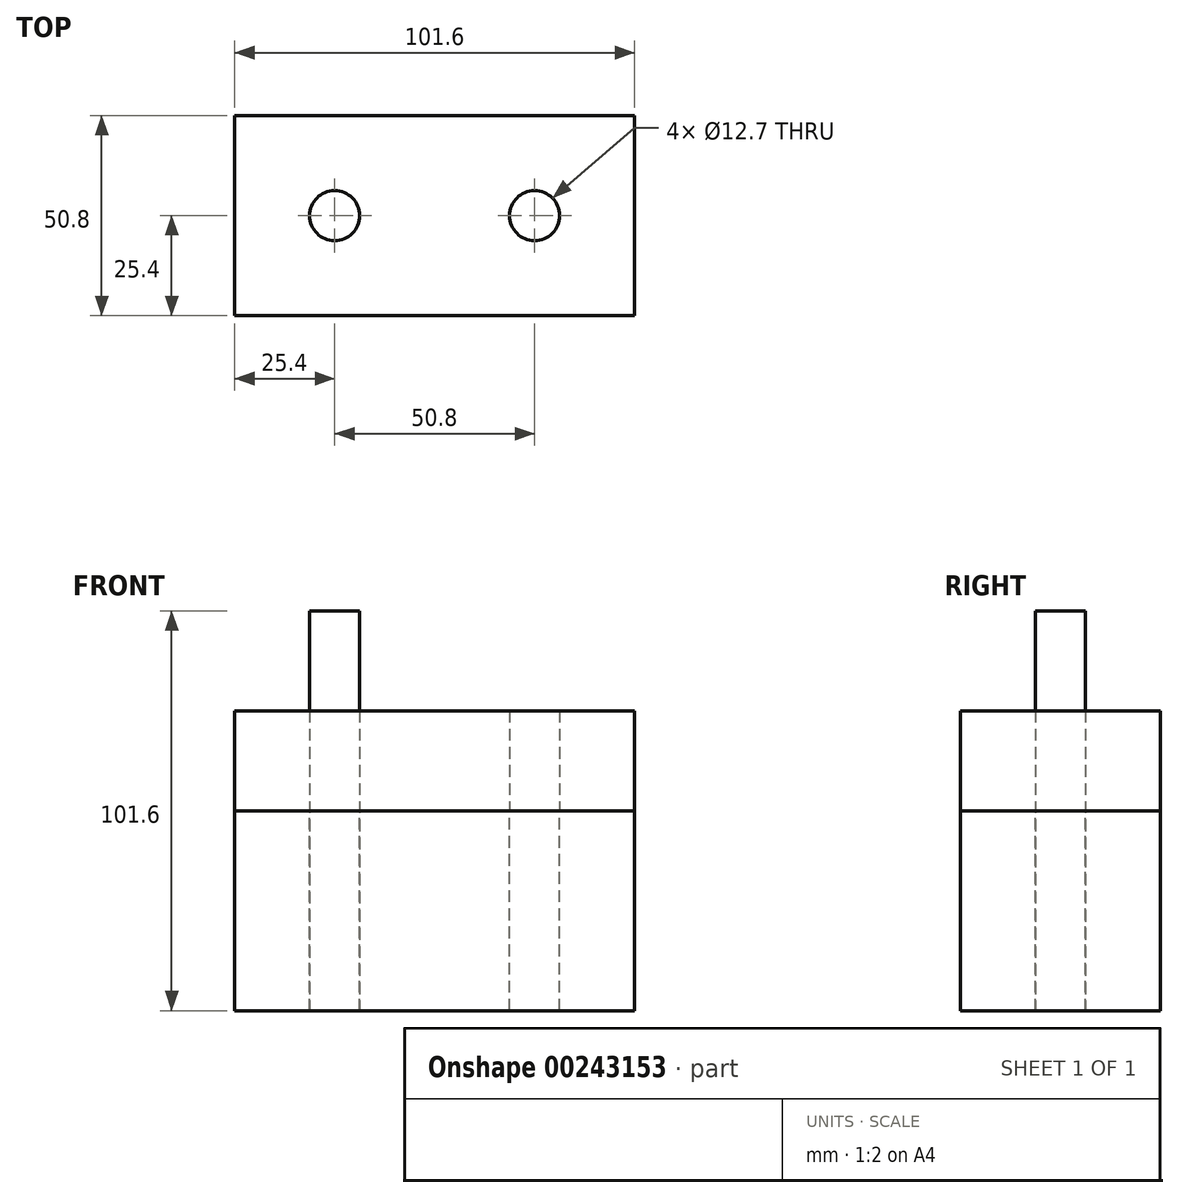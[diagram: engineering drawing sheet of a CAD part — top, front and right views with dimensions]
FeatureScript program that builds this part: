
annotation { "Feature Type Name" : "Feature", "Feature Type Description" : "" }
export const myFeature = defineFeature(function(context is Context, id is Id, definition is map)
    precondition{}
    {
        {
            var Q0;
            Q0=qCreatedBy(makeId("Top.planeOp"),FACE);
            var sketch = newSketch(context, id + "F0", { "sketchPlane" : qUnion([Q0])});
            skLineSegment(sketch, "E0.bottom", {"start": v(0, 0) * mm, "end": v(101.6, 0) * mm});
            skLineSegment(sketch, "E0.top", {"start": v(0, 50.8) * mm, "end": v(101.6, 50.8) * mm});
            skLineSegment(sketch, "E0.left", {"start": v(0, 0) * mm, "end": v(0, 50.8) * mm});
            skLineSegment(sketch, "E0.right", {"start": v(101.6, 0) * mm, "end": v(101.6, 50.8) * mm});
            skCircle(sketch, "E1", {"center": v(25.4, 25.4) * mm, "radius": 6.35 * mm});
            skPoint(sketch, "E1.centerSnap0", {"position": v(0, 25.4) * mm});
            skCircle(sketch, "E2", {"center": v(76.2, 25.4) * mm, "radius": 6.35 * mm});
            skSolve(sketch);
        }
        {
            var Q0;
            Q0 = qSketchRegion(id + "F0", true);
            extrude(context, id + "F1", {"entities" : qUnion([Q0]), "depth" : 25.4 * mm});
        }
        {
            var Q0;
            Q0 = qSketchRegion(id + "F0", true);
            extrude(context, id + "F2", {"entities" : qUnion([Q0]), "oppositeDirection" : true, "depth" : 50.8 * mm});
        }
        {
            var Q0;
            Q0=makeQuery(id+"F2.opExtrude","CAP_FACE",FACE,{"disambiguationData":[OSD([sQuery(id+"F0.wireOp",EDGE,"E0.bottom"),sQuery(id+"F0.wireOp",EDGE,"E0.top"),sQuery(id+"F0.wireOp",EDGE,"E0.left"),sQuery(id+"F0.wireOp",EDGE,"E0.right"),sQuery(id+"F0.wireOp",EDGE,"E1"),sQuery(id+"F0.wireOp",EDGE,"E2")])],"isStart":false});
            var sketch = newSketch(context, id + "F3", { "sketchPlane" : qUnion([Q0])});
            skCircle(sketch, "E3.0", {"center": v(25.4, -25.4) * mm, "radius": 6.35 * mm});
            skSolve(sketch);
        }
        {
            var Q0;
            Q0 = qSketchRegion(id + "F3", true);
            extrude(context, id + "F4", {"entities" : qUnion([Q0]), "oppositeDirection" : true, "depth" : 101.6 * mm});
        }
    });
